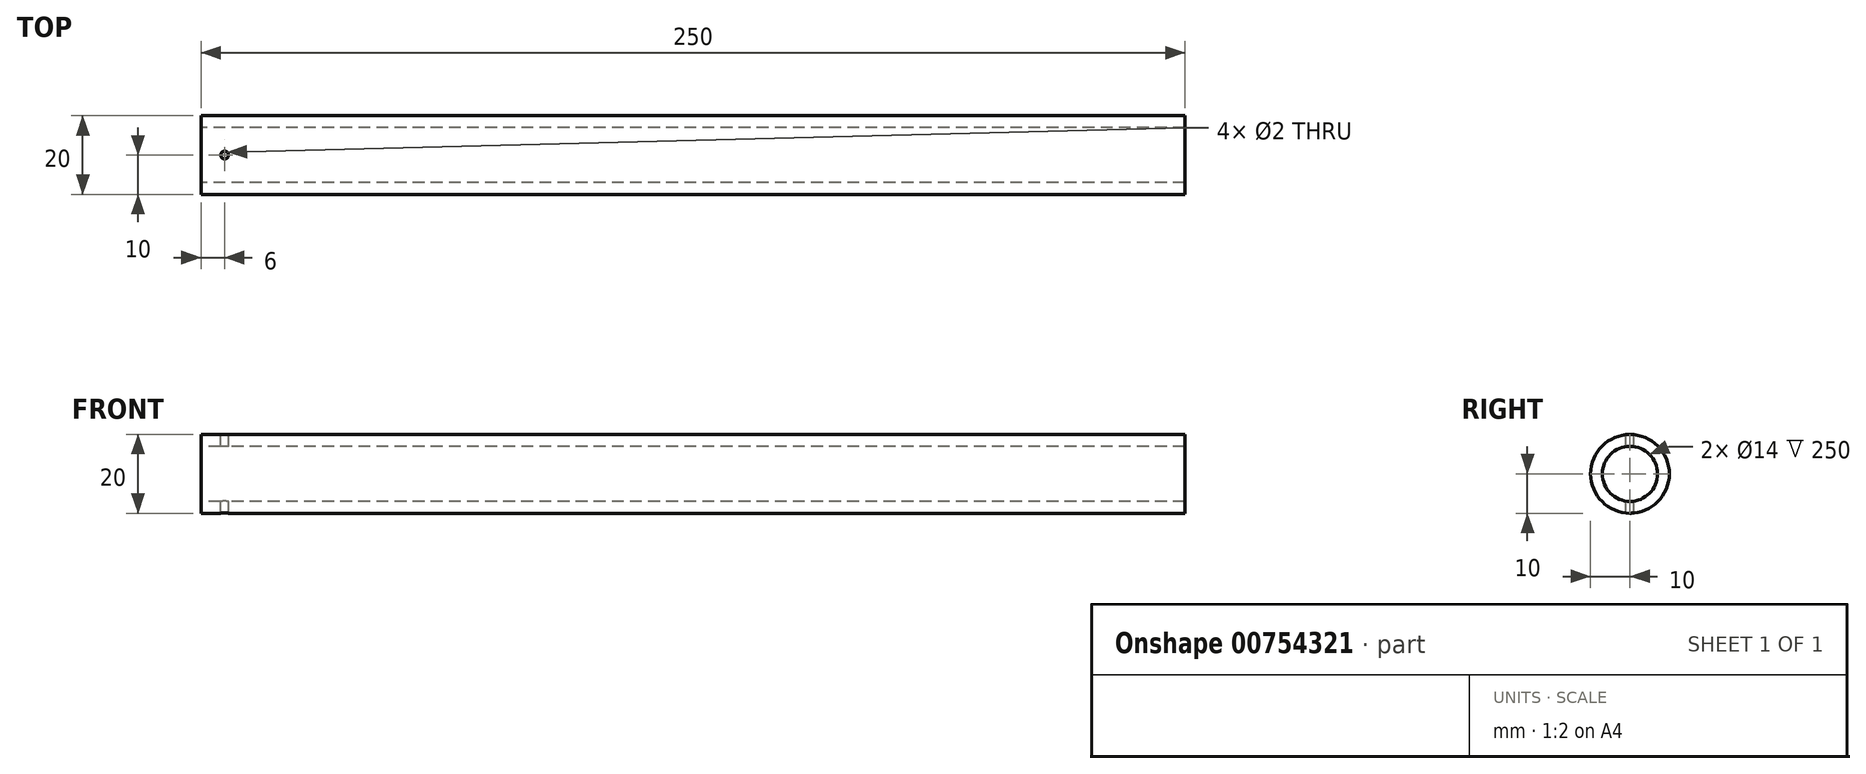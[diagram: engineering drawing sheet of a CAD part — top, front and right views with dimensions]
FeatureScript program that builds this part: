
annotation { "Feature Type Name" : "Feature", "Feature Type Description" : "" }
export const myFeature = defineFeature(function(context is Context, id is Id, definition is map)
    precondition{}
    {
        {
            var Q0;
            Q0=qCreatedBy(makeId("Right.planeOp"),FACE);
            var sketch = newSketch(context, id + "F0", { "sketchPlane" : qUnion([Q0])});
            skCircle(sketch, "E0", {"center": v(0, 0) * mm, "radius": 10 * mm});
            skCircle(sketch, "E1", {"center": v(0, 0) * mm, "radius": 7 * mm});
            skSolve(sketch);
        }
        {
            var Q0;
            Q0=makeQuery(id+"F0.imprint","IMPRINT",FACE,{"disambiguationData":[TD([[makeQuery(id+"F0.imprint","IMPRINT",EDGE,{"derivedFrom":sQuery(id+"F0.wireOp",EDGE,"E0")}),1.0]])]});
            extrude(context, id + "F1", {"entities" : qUnion([Q0]), "depth" : 250 * mm, "offsetDistance" : 25 * mm});
        }
        {
            var Q0;
            Q0=qCreatedBy(makeId("Top.planeOp"),FACE);
            var sketch = newSketch(context, id + "F2", { "sketchPlane" : qUnion([Q0])});
            skCircle(sketch, "E2", {"center": v(6, 0) * mm, "radius": 1 * mm});
            skLineSegment(sketch, "E3", {"start": v(6, 0) * mm, "end": v(0, 0) * mm, "construction": true});
            skSolve(sketch);
        }
        {
            var Q0;
            Q0 = qSketchRegion(id + "F2", true);
            extrude(context, id + "F3", {"entities" : qUnion([Q0]), "operationType" : NewBodyOperationType.REMOVE, "oppositeDirection" : true, "depth" : 25 * mm, "offsetDistance" : 25 * mm, "symmetric" : true});
        }
    });
